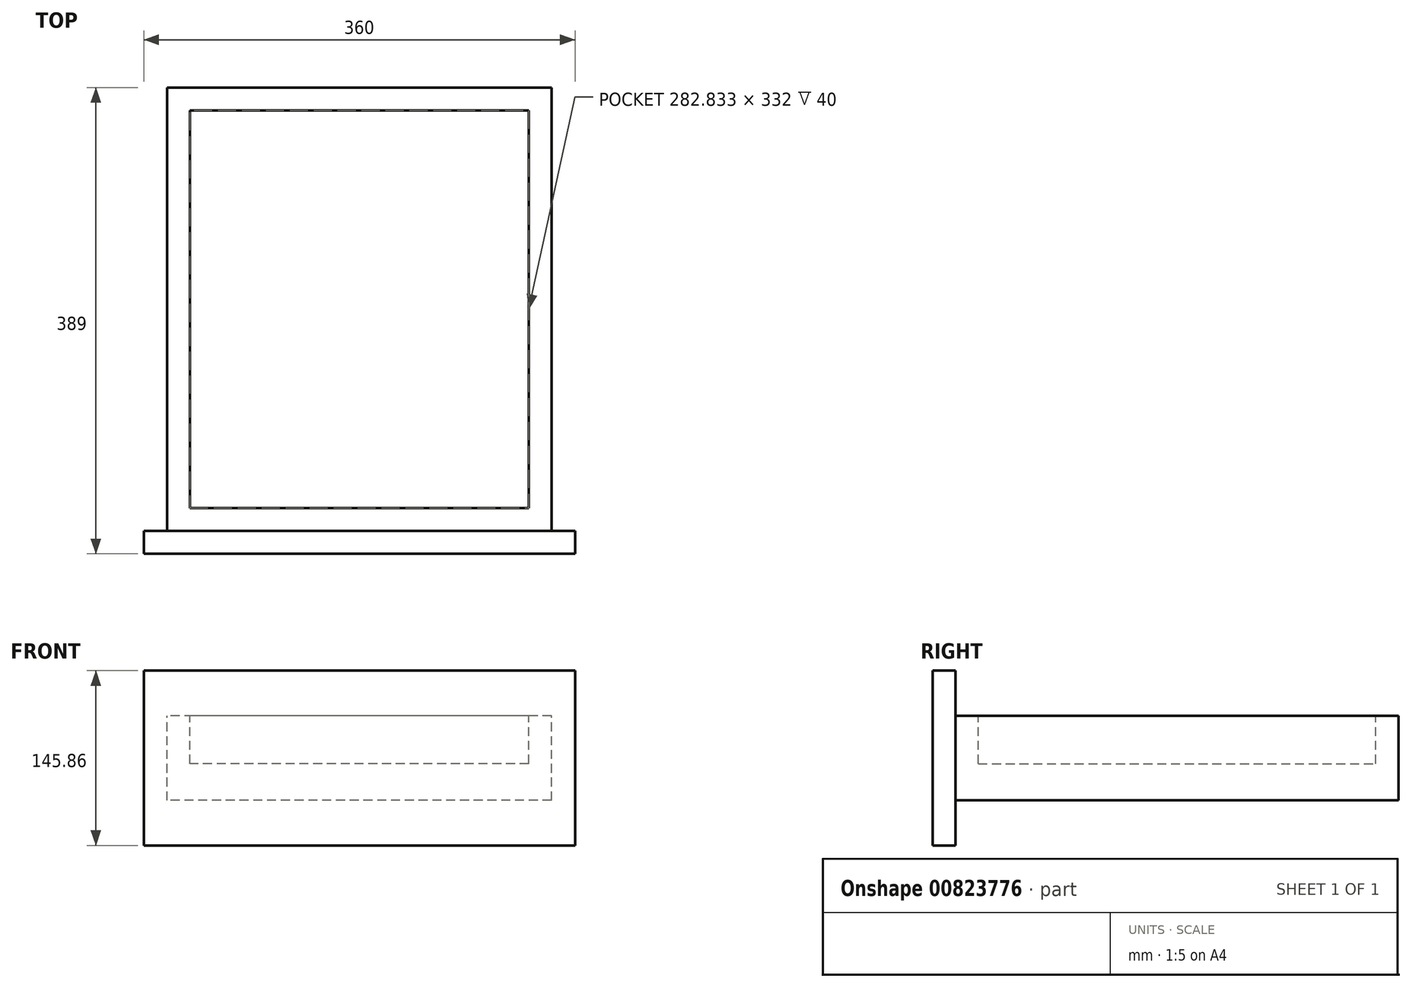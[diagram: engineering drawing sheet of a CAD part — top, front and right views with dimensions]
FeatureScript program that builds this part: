
annotation { "Feature Type Name" : "Feature", "Feature Type Description" : "" }
export const myFeature = defineFeature(function(context is Context, id is Id, definition is map)
    precondition{}
    {
        {
            var Q0;
            Q0=qCreatedBy(makeId("Front.planeOp"),FACE);
            var sketch = newSketch(context, id + "F0", { "sketchPlane" : qUnion([Q0])});
            skLineSegment(sketch, "E0.bottom", {"start": v(160.42, -35.31) * mm, "end": v(-160.42, -35.31) * mm});
            skLineSegment(sketch, "E0.top", {"start": v(160.42, 35.31) * mm, "end": v(-160.42, 35.31) * mm});
            skLineSegment(sketch, "E0.left", {"start": v(160.42, -35.31) * mm, "end": v(160.42, 35.31) * mm});
            skLineSegment(sketch, "E0.right", {"start": v(-160.42, -35.31) * mm, "end": v(-160.42, 35.31) * mm});
            skPoint(sketch, "E0.middle", {"position": v(0, 0) * mm});
            skSolve(sketch);
        }
        {
            var Q0;
            Q0=makeQuery(id+"F0.imprint","IMPRINT",FACE,{"disambiguationData":[TD([[makeQuery(id+"F0.imprint","IMPRINT",EDGE,{"derivedFrom":sQuery(id+"F0.wireOp",EDGE,"E0.bottom")}),-1.0]])]});
            extrude(context, id + "F1", {"entities" : qUnion([Q0]), "depth" : 370 * mm, "offsetDistance" : 25 * mm});
        }
        {
            var Q0;
            Q0=makeQuery(id+"F1.opExtrude","SWEPT_FACE",FACE,{"disambiguationData":[OSD([sQuery(id+"F0.wireOp",EDGE,"E0.top")])]});
            var sketch = newSketch(context, id + "F2", { "sketchPlane" : qUnion([Q0])});
            skLineSegment(sketch, "E1.bottom", {"start": v(-141.42, -19) * mm, "end": v(141.42, -19) * mm});
            skLineSegment(sketch, "E1.top", {"start": v(-141.42, -351) * mm, "end": v(141.42, -351) * mm});
            skLineSegment(sketch, "E1.left", {"start": v(-141.42, -19) * mm, "end": v(-141.42, -351) * mm});
            skLineSegment(sketch, "E1.right", {"start": v(141.42, -19) * mm, "end": v(141.42, -351) * mm});
            skSolve(sketch);
        }
        {
            var Q0;
            Q0=makeQuery(id+"F2.imprint","IMPRINT",FACE,{"disambiguationData":[TD([[makeQuery(id+"F2.imprint","IMPRINT",EDGE,{"derivedFrom":sQuery(id+"F2.wireOp",EDGE,"E1.bottom")}),-1.0]])]});
            extrude(context, id + "F3", {"entities" : qUnion([Q0]), "operationType" : NewBodyOperationType.ADD, "oppositeDirection" : true, "depth" : 40 * mm, "offsetDistance" : 25 * mm});
        }
        {
            var Q0;
            Q0=makeQuery(id+"F1.opExtrude","SWEPT_FACE",FACE,{"disambiguationData":[OSD([sQuery(id+"F0.wireOp",EDGE,"E0.top")])]});
            var sketch = newSketch(context, id + "F4", { "sketchPlane" : qUnion([Q0])});
            skLineSegment(sketch, "E2.bottom", {"start": v(141.42, -351) * mm, "end": v(-141.42, -351) * mm});
            skLineSegment(sketch, "E2.top", {"start": v(141.42, -19) * mm, "end": v(-141.42, -19) * mm});
            skLineSegment(sketch, "E2.left", {"start": v(141.42, -351) * mm, "end": v(141.42, -19) * mm});
            skLineSegment(sketch, "E2.right", {"start": v(-141.42, -351) * mm, "end": v(-141.42, -19) * mm});
            skPoint(sketch, "E2.middle", {"position": v(0, -185) * mm});
            skSolve(sketch);
        }
        {
            var Q0;
            Q0=makeQuery(id+"F4.imprint","IMPRINT",FACE,{"disambiguationData":[TD([[makeQuery(id+"F4.imprint","IMPRINT",EDGE,{"derivedFrom":sQuery(id+"F4.wireOp",EDGE,"E2.bottom")}),-1.0]])]});
            extrude(context, id + "F5", {"entities" : qUnion([Q0]), "operationType" : NewBodyOperationType.REMOVE, "oppositeDirection" : true, "depth" : 40 * mm, "offsetDistance" : 25 * mm});
        }
        {
            var Q0;
            Q0=makeQuery(id+"F1.opExtrude","CAP_FACE",FACE,{"disambiguationData":[OSD([sQuery(id+"F0.wireOp",EDGE,"E0.bottom"),sQuery(id+"F0.wireOp",EDGE,"E0.top"),sQuery(id+"F0.wireOp",EDGE,"E0.left"),sQuery(id+"F0.wireOp",EDGE,"E0.right")])],"isStart":false});
            var sketch = newSketch(context, id + "F6", { "sketchPlane" : qUnion([Q0])});
            skLineSegment(sketch, "E3.bottom", {"start": v(-180, 72.93) * mm, "end": v(180, 72.93) * mm});
            skLineSegment(sketch, "E3.top", {"start": v(-180, -72.93) * mm, "end": v(180, -72.93) * mm});
            skLineSegment(sketch, "E3.left", {"start": v(-180, 72.93) * mm, "end": v(-180, -72.93) * mm});
            skLineSegment(sketch, "E3.right", {"start": v(180, 72.93) * mm, "end": v(180, -72.93) * mm});
            skPoint(sketch, "E3.middle", {"position": v(0, 0) * mm});
            skSolve(sketch);
        }
        {
            var Q0;
            Q0=makeQuery(id+"F6.imprint","IMPRINT",FACE,{"disambiguationData":[TD([[makeQuery(id+"F6.imprint","IMPRINT",EDGE,{"derivedFrom":sQuery(id+"F6.wireOp",EDGE,"E3.bottom")}),-1.0]])]});
            var Q1;
            Q1=makeQuery(id+"F6.imprint","IMPRINT",FACE,{"disambiguationData":[TD([[makeQuery(id+"F6.imprint","IMPRINT",EDGE,{"derivedFrom":makeQuery(id+"F1.opExtrude","CAP_EDGE",EDGE,{"disambiguationData":[OSD([sQuery(id+"F0.wireOp",EDGE,"E0.bottom")])],"isStart":false})}),-1.0]])]});
            extrude(context, id + "F7", {"entities" : qUnion([Q0, Q1]), "operationType" : NewBodyOperationType.ADD, "depth" : 19 * mm, "offsetDistance" : 25 * mm});
        }
    });
